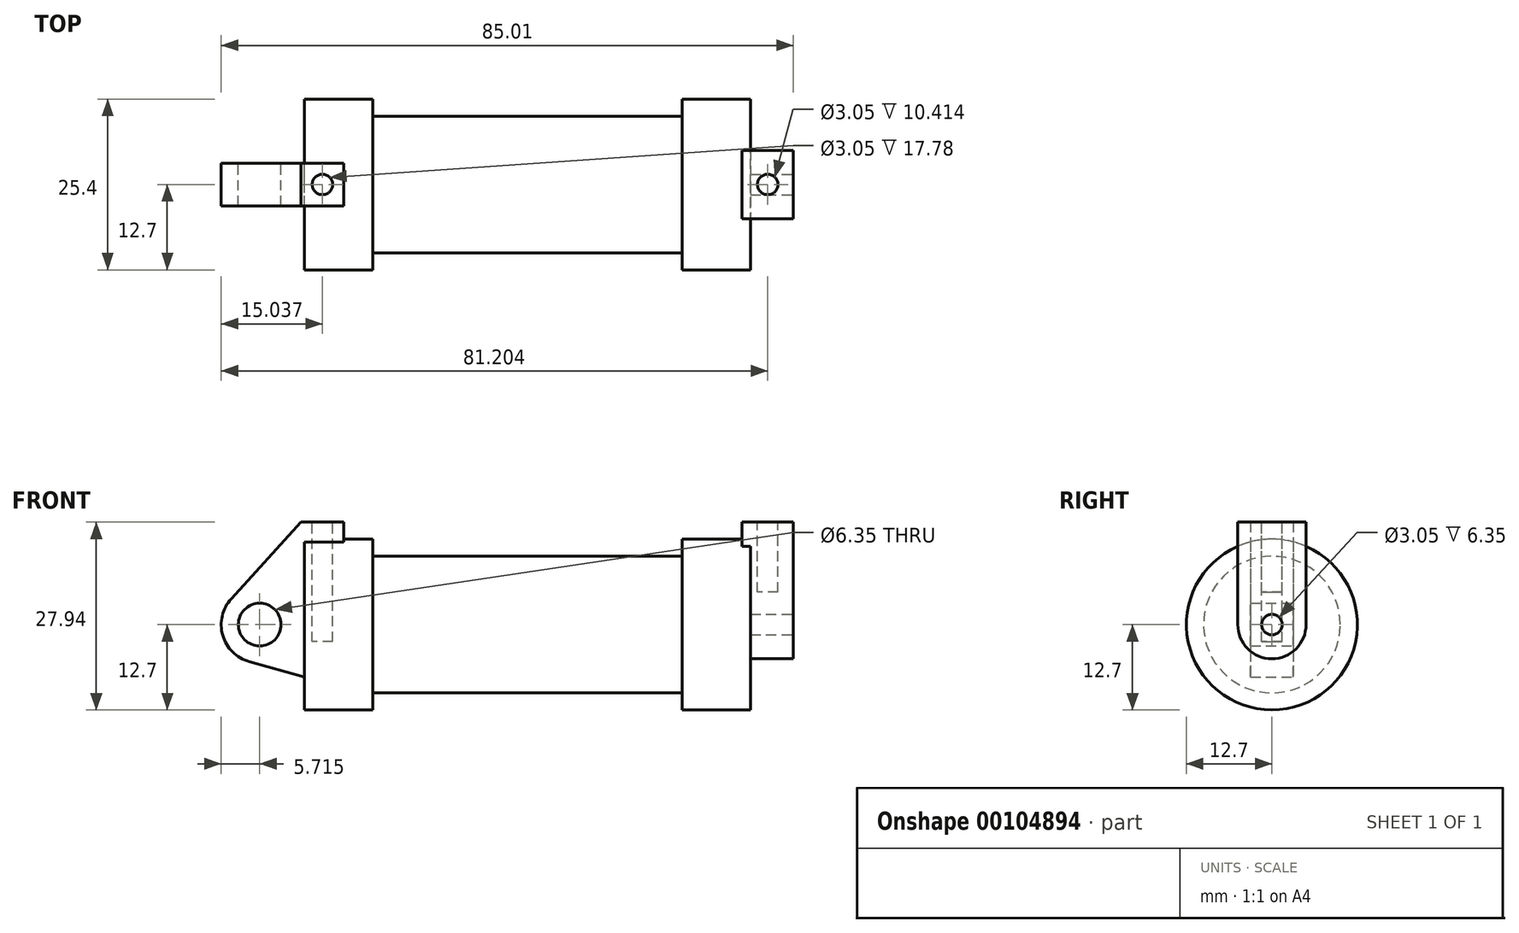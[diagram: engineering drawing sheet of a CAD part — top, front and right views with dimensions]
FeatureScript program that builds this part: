
annotation { "Feature Type Name" : "Feature", "Feature Type Description" : "" }
export const myFeature = defineFeature(function(context is Context, id is Id, definition is map)
    precondition{}
    {
        {
            var Q0;
            Q0=qCreatedBy(makeId("Front.planeOp"),FACE);
            var sketch = newSketch(context, id + "F0", { "sketchPlane" : qUnion([Q0])});
            skLineSegment(sketch, "E0", {"start": v(0, 0) * mm, "end": v(0, 12.7) * mm});
            skLineSegment(sketch, "E1", {"start": v(0, 12.7) * mm, "end": v(10.16, 12.7) * mm});
            skLineSegment(sketch, "E2", {"start": v(10.16, 12.7) * mm, "end": v(10.16, 10.16) * mm});
            skLineSegment(sketch, "E3", {"start": v(10.16, 10.16) * mm, "end": v(56.13, 10.16) * mm});
            skLineSegment(sketch, "E4", {"start": v(56.13, 10.16) * mm, "end": v(56.13, 12.7) * mm});
            skLineSegment(sketch, "E5", {"start": v(56.13, 12.7) * mm, "end": v(66.3, 12.7) * mm});
            skLineSegment(sketch, "E6", {"start": v(66.3, 12.7) * mm, "end": v(66.3, 0) * mm});
            skLineSegment(sketch, "E7", {"start": v(66.3, 0) * mm, "end": v(0, 0) * mm});
            skLineSegment(sketch, "E8", {"start": v(5.84, 15.24) * mm, "end": v(-0.5, 15.24) * mm});
            skLineSegment(sketch, "E9", {"start": v(-0.5, 15.24) * mm, "end": v(-10.88, 3.85) * mm});
            skLineSegment(sketch, "E10", {"start": v(0, 0) * mm, "end": v(-6.65, 0) * mm});
            skCircle(sketch, "E11", {"center": v(-6.65, 0) * mm, "radius": 5.72 * mm});
            skCircle(sketch, "E12", {"center": v(-6.65, 0) * mm, "radius": 3.18 * mm});
            skLineSegment(sketch, "E13", {"start": v(5.84, 15.24) * mm, "end": v(5.84, -9.4) * mm});
            skLineSegment(sketch, "E14", {"start": v(5.84, -9.4) * mm, "end": v(-8.18, -5.5) * mm});
            skSolve(sketch);
        }
        {
            var Q0;
            {var subQ0=sQuery(id+"F0.wireOp",EDGE,"E2");Q0=makeQuery(id+"F0.imprint","IMPRINT",FACE,{"disambiguationData":[TD([[makeQuery(id+"F0.imprint","IMPRINT",EDGE,{"derivedFrom":subQ0}),-1.0]])]});}
            var Q1;
            {var subQ0=sQuery(id+"F0.wireOp",EDGE,"E0");Q1=makeQuery(id+"F0.imprint","IMPRINT",FACE,{"disambiguationData":[TD([[makeQuery(id+"F0.imprint","IMPRINT",EDGE,{"derivedFrom":subQ0}),-1.0]])]});}
            var Q2;
            Q2=sQuery(id+"F0.wireOp",EDGE,"E7");
            revolve(context, id + "F1", {"entities" : qUnion([Q0, Q1]), "axis" : qUnion([Q2]), "revolveType" : RevolveType.FULL});
        }
        {
            var Q0;
            {var subQ0=sQuery(id+"F0.wireOp",EDGE,"E0");Q0=makeQuery(id+"F0.imprint","IMPRINT",FACE,{"disambiguationData":[TD([[makeQuery(id+"F0.imprint","IMPRINT",EDGE,{"derivedFrom":subQ0}),-1.0]])]});}
            var Q1;
            {var subQ3=sQuery(id+"F0.wireOp",EDGE,"E0");Q1=makeQuery(id+"F0.imprint","IMPRINT",FACE,{"disambiguationData":[TD([[makeQuery(id+"F0.imprint","IMPRINT",EDGE,{"derivedFrom":subQ3}),1.0]])]});}
            var Q2;
            {var subQ4=sQuery(id+"F0.wireOp",EDGE,"E12");Q2=makeQuery(id+"F0.imprint","IMPRINT",FACE,{"disambiguationData":[TD([[makeQuery(id+"F0.imprint","IMPRINT",EDGE,{"derivedFrom":subQ4}),-1.0]])]});}
            var Q3;
            {var subQ0=sQuery(id+"F0.wireOp",EDGE,"E14");Q3=makeQuery(id+"F0.imprint","IMPRINT",FACE,{"disambiguationData":[TD([[makeQuery(id+"F0.imprint","IMPRINT",EDGE,{"derivedFrom":subQ0}),-1.0]])]});}
            extrude(context, id + "F2", {"entities" : qUnion([Q0, Q1, Q2, Q3]), "operationType" : NewBodyOperationType.ADD, "endBound" : BoundingType.SYMMETRIC, "depth" : 6.35 * mm});
        }
        {
            var Q0;
            Q0=makeQuery(id+"F1.opRevolve","SWEPT_FACE",FACE,{"disambiguationData":[OSD([sQuery(id+"F0.wireOp",EDGE,"E6")])]});
            var sketch = newSketch(context, id + "F3", { "sketchPlane" : qUnion([Q0])});
            skCircle(sketch, "E15", {"center": v(0, 0) * mm, "radius": 1.52 * mm});
            skCircle(sketch, "E16", {"center": v(0, 0) * mm, "radius": 5.08 * mm});
            skLineSegment(sketch, "E17", {"start": v(-5.08, 0) * mm, "end": v(-5.08, 15.24) * mm});
            skLineSegment(sketch, "E18", {"start": v(5.08, 15.4) * mm, "end": v(5.08, 0) * mm});
            skLineSegment(sketch, "E19", {"start": v(-5.08, 15.24) * mm, "end": v(5.08, 15.24) * mm});
            skSolve(sketch);
        }
        {
            var Q0;
            Q0 = qSketchRegion(id + "F3", true);
            extrude(context, id + "F4", {"entities" : qUnion([Q0]), "operationType" : NewBodyOperationType.ADD, "oppositeDirection" : true, "depth" : 1.27 * mm, "hasSecondDirection" : true, "secondDirectionOppositeDirection" : false, "secondDirectionDepth" : 6.35 * mm});
        }
        {
            var Q0;
            Q0=makeQuery(id+"F4.opExtrude","SWEPT_FACE",FACE,{"disambiguationData":[OSD([sQuery(id+"F3.wireOp",EDGE,"E19")])]});
            var sketch = newSketch(context, id + "F5", { "sketchPlane" : qUnion([Q0])});
            skCircle(sketch, "E20", {"center": v(68.83, 0) * mm, "radius": 1.52 * mm});
            skPoint(sketch, "E20.centerSnap0", {"position": v(68.83, -5.08) * mm});
            skPoint(sketch, "E20.centerSnap1", {"position": v(72.64, 0) * mm});
            skSolve(sketch);
        }
        {
            var Q0;
            Q0 = qSketchRegion(id + "F5", true);
            extrude(context, id + "F6", {"entities" : qUnion([Q0]), "operationType" : NewBodyOperationType.REMOVE, "oppositeDirection" : true, "depth" : 10.4 * mm});
        }
        {
            var Q0;
            Q0=makeQuery(id+"F2.opExtrude","SWEPT_FACE",FACE,{"disambiguationData":[OSD([sQuery(id+"F0.wireOp",EDGE,"E8")])]});
            var sketch = newSketch(context, id + "F7", { "sketchPlane" : qUnion([Q0])});
            skCircle(sketch, "E21", {"center": v(2.67, 0) * mm, "radius": 1.52 * mm});
            skPoint(sketch, "E21.centerSnap0", {"position": v(2.67, -3.18) * mm});
            skPoint(sketch, "E21.centerSnap1", {"position": v(5.84, 0) * mm});
            skSolve(sketch);
        }
        {
            var Q0;
            Q0=makeQuery(id+"F7.imprint","IMPRINT",FACE,{"disambiguationData":[TD([[makeQuery(id+"F7.imprint","IMPRINT",EDGE,{"derivedFrom":sQuery(id+"F7.wireOp",EDGE,"E21")}),1.0]])]});
            extrude(context, id + "F8", {"entities" : qUnion([Q0]), "operationType" : NewBodyOperationType.REMOVE, "oppositeDirection" : true, "depth" : 17.78 * mm});
        }
        {
            var Q0;
            Q0=makeQuery(id+"F4.boolean.opBoolean","SPLIT",FACE,{"disambiguationData":[TD([makeQuery(id+"F4.opExtrude","SWEPT_FACE",FACE,{"disambiguationData":[OSD([sQuery(id+"F3.wireOp",EDGE,"E15")])]})])],"derivedFrom":makeQuery(id+"F1.opRevolve","SWEPT_FACE",FACE,{"disambiguationData":[OSD([sQuery(id+"F0.wireOp",EDGE,"E6")])]})});
            var Q1;
            Q1=makeQuery(id+"F1.opRevolve","SWEPT_FACE",FACE,{"disambiguationData":[OSD([sQuery(id+"F0.wireOp",EDGE,"E2")])]});
            extrude(context, id + "F9", {"entities" : qUnion([Q0]), "operationType" : NewBodyOperationType.ADD, "endBound" : BoundingType.UP_TO_SURFACE, "oppositeDirection" : true, "endBoundEntityFace" : qUnion([Q1]), "depth" : 25.4 * mm});
        }
    });
